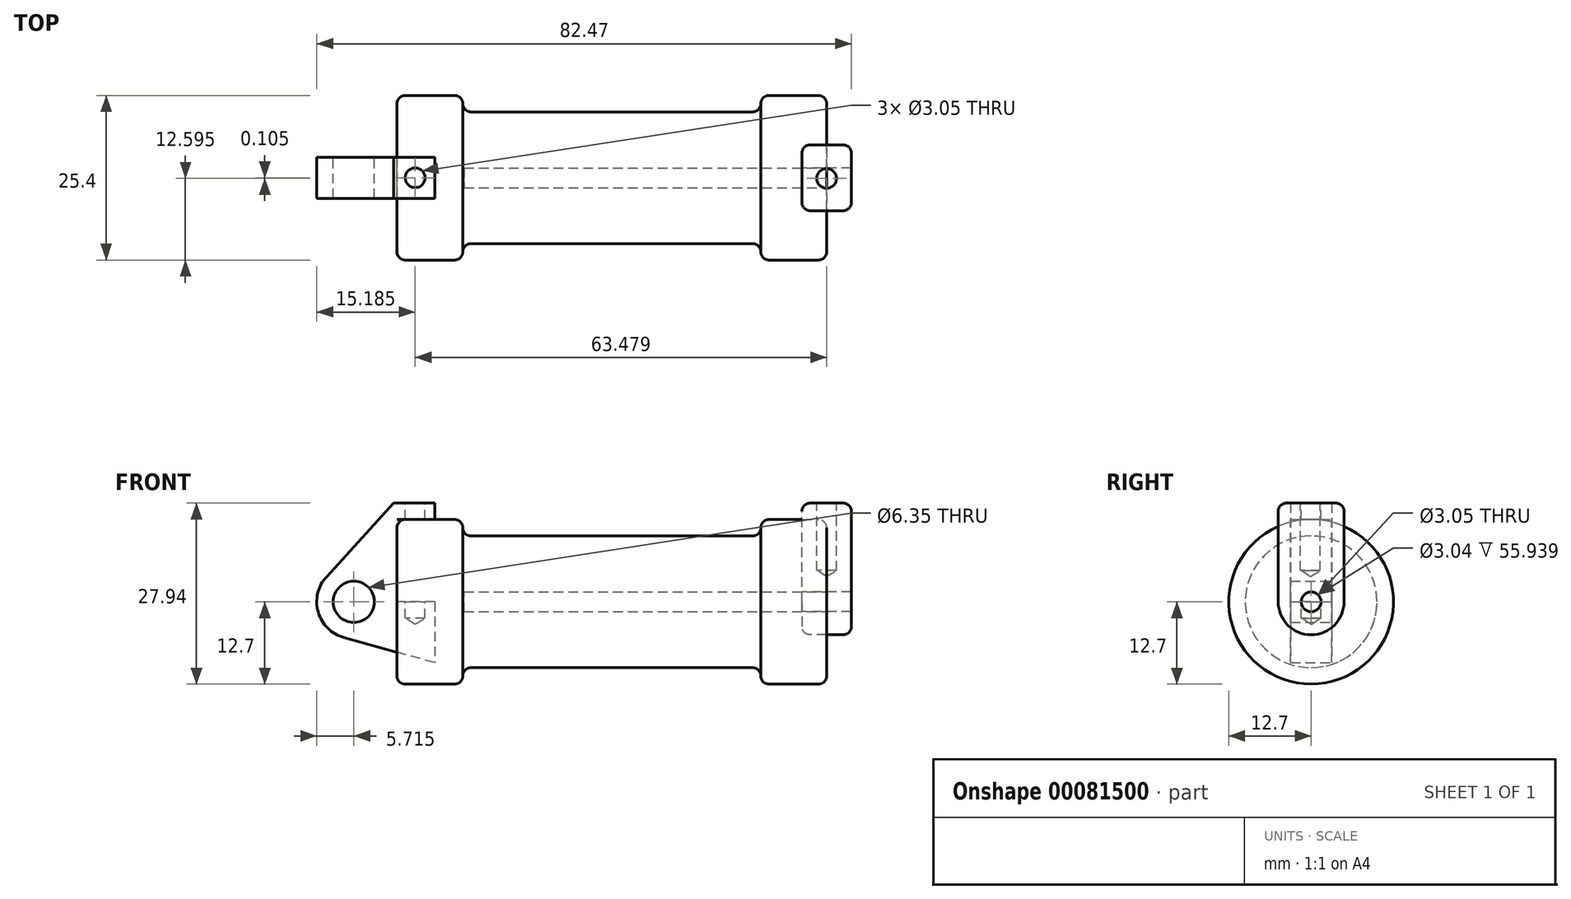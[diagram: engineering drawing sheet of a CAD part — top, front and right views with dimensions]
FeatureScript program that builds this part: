
annotation { "Feature Type Name" : "Feature", "Feature Type Description" : "" }
export const myFeature = defineFeature(function(context is Context, id is Id, definition is map)
    precondition{}
    {
        {
            var Q0;
            Q0=qCreatedBy(makeId("Front.planeOp"),FACE);
            var sketch = newSketch(context, id + "F0", { "sketchPlane" : qUnion([Q0])});
            skLineSegment(sketch, "E0", {"start": v(0, 0) * mm, "end": v(0, 12.7) * mm});
            skLineSegment(sketch, "E1", {"start": v(0, 12.7) * mm, "end": v(10.16, 12.7) * mm});
            skLineSegment(sketch, "E2", {"start": v(10.16, 12.7) * mm, "end": v(10.16, 10.16) * mm});
            skLineSegment(sketch, "E3", {"start": v(10.16, 10.16) * mm, "end": v(56.13, 10.16) * mm});
            skLineSegment(sketch, "E4", {"start": v(56.13, 10.16) * mm, "end": v(56.13, 12.7) * mm});
            skLineSegment(sketch, "E5", {"start": v(56.13, 12.7) * mm, "end": v(66.3, 12.7) * mm});
            skLineSegment(sketch, "E6", {"start": v(66.3, 12.7) * mm, "end": v(66.3, 0) * mm});
            skLineSegment(sketch, "E7", {"start": v(66.3, 0) * mm, "end": v(0, 0) * mm});
            skLineSegment(sketch, "E8", {"start": v(5.84, 15.24) * mm, "end": v(-0.5, 15.24) * mm});
            skLineSegment(sketch, "E9", {"start": v(-0.5, 15.24) * mm, "end": v(-10.88, 3.85) * mm});
            skLineSegment(sketch, "E10", {"start": v(0, 0) * mm, "end": v(-6.65, 0) * mm});
            skCircle(sketch, "E11", {"center": v(-6.65, 0) * mm, "radius": 5.72 * mm});
            skCircle(sketch, "E12", {"center": v(-6.65, 0) * mm, "radius": 3.18 * mm});
            skLineSegment(sketch, "E13", {"start": v(5.84, 15.24) * mm, "end": v(5.84, -9.4) * mm});
            skLineSegment(sketch, "E14", {"start": v(5.84, -9.4) * mm, "end": v(-8.18, -5.5) * mm});
            skSolve(sketch);
        }
        {
            var Q0;
            {var subQ0=sQuery(id+"F0.wireOp",EDGE,"E2");Q0=makeQuery(id+"F0.imprint","IMPRINT",FACE,{"disambiguationData":[TD([[makeQuery(id+"F0.imprint","IMPRINT",EDGE,{"derivedFrom":subQ0}),-1.0]])]});}
            var Q1;
            {var subQ0=sQuery(id+"F0.wireOp",EDGE,"E0");Q1=makeQuery(id+"F0.imprint","IMPRINT",FACE,{"disambiguationData":[TD([[makeQuery(id+"F0.imprint","IMPRINT",EDGE,{"derivedFrom":subQ0}),-1.0]])]});}
            var Q2;
            Q2=sQuery(id+"F0.wireOp",EDGE,"E7");
            revolve(context, id + "F1", {"entities" : qUnion([Q0, Q1]), "axis" : qUnion([Q2]), "revolveType" : RevolveType.FULL});
        }
        {
            var Q0;
            {var subQ3=sQuery(id+"F0.wireOp",EDGE,"E0");Q0=makeQuery(id+"F0.imprint","IMPRINT",FACE,{"disambiguationData":[TD([[makeQuery(id+"F0.imprint","IMPRINT",EDGE,{"derivedFrom":subQ3}),1.0]])]});}
            var Q1;
            {var subQ0=sQuery(id+"F0.wireOp",EDGE,"E14");Q1=makeQuery(id+"F0.imprint","IMPRINT",FACE,{"disambiguationData":[TD([[makeQuery(id+"F0.imprint","IMPRINT",EDGE,{"derivedFrom":subQ0}),-1.0]])]});}
            var Q2;
            {var subQ4=sQuery(id+"F0.wireOp",EDGE,"E12");Q2=makeQuery(id+"F0.imprint","IMPRINT",FACE,{"disambiguationData":[TD([[makeQuery(id+"F0.imprint","IMPRINT",EDGE,{"derivedFrom":subQ4}),-1.0]])]});}
            extrude(context, id + "F2", {"entities" : qUnion([Q0, Q1, Q2]), "endBound" : BoundingType.SYMMETRIC, "depth" : 6.35 * mm});
        }
        {
            var Q0;
            Q0=makeQuery(id+"F1.opRevolve","SWEPT_FACE",FACE,{"disambiguationData":[OSD([sQuery(id+"F0.wireOp",EDGE,"E6")])]});
            var sketch = newSketch(context, id + "F3", { "sketchPlane" : qUnion([Q0])});
            skCircle(sketch, "E15", {"center": v(0, 0) * mm, "radius": 5.08 * mm});
            skCircle(sketch, "E16", {"center": v(0, 0) * mm, "radius": 1.52 * mm});
            skLineSegment(sketch, "E17", {"start": v(-5.08, 0) * mm, "end": v(-5.08, 15.24) * mm});
            skLineSegment(sketch, "E18", {"start": v(5.08, 0) * mm, "end": v(5.08, 15.24) * mm});
            skLineSegment(sketch, "E19", {"start": v(-5.08, 15.24) * mm, "end": v(5.08, 15.24) * mm});
            skSolve(sketch);
        }
        {
            var Q0;
            Q0=makeQuery(id+"F3.imprint","IMPRINT",FACE,{"disambiguationData":[TD([[makeQuery(id+"F3.imprint","IMPRINT",EDGE,{"derivedFrom":sQuery(id+"F3.wireOp",EDGE,"E16")}),-1.0]])]});
            var Q1;
            {var subQ0=sQuery(id+"F3.wireOp",EDGE,"E19");Q1=makeQuery(id+"F3.imprint","IMPRINT",FACE,{"disambiguationData":[TD([[makeQuery(id+"F3.imprint","IMPRINT",EDGE,{"derivedFrom":subQ0}),-1.0]])]});}
            var Q2;
            {var subQ0=sQuery(id+"F3.wireOp",EDGE,"E17");var subQ1=sQuery(id+"F3.wireOp",EDGE,"E15");var subQ2=makeQuery(id+"F3.imprint","INTERSECT",VERTEX,{"derivedFrom":[subQ1,subQ0]});Q2=makeQuery(id+"F3.imprint","IMPRINT",FACE,{"disambiguationData":[TD([[makeQuery(id+"F3.imprint","IMPRINT",EDGE,{"disambiguationData":[TD([[subQ2,1.0]])],"derivedFrom":subQ1}),-1.0]])]});}
            extrude(context, id + "F4", {"entities" : qUnion([Q0, Q1, Q2]), "endBound" : BoundingType.SYMMETRIC, "depth" : 7.62 * mm});
        }
        {
            var Q0;
            Q0=makeQuery(id+"F4.opExtrude","CAP_FACE",FACE,{"disambiguationData":[OSD([sQuery(id+"F3.wireOp",EDGE,"E15"),sQuery(id+"F3.wireOp",EDGE,"E16"),sQuery(id+"F3.wireOp",EDGE,"E17"),sQuery(id+"F3.wireOp",EDGE,"E18"),sQuery(id+"F3.wireOp",EDGE,"E19")])],"isStart":false});
            var sketch = newSketch(context, id + "F5", { "sketchPlane" : qUnion([Q0])});
            skCircle(sketch, "E20", {"center": v(0, 0) * mm, "radius": 1.52 * mm});
            skSolve(sketch);
        }
        {
            var Q0;
            Q0 = qSketchRegion(id + "F5", true);
            extrude(context, id + "F6", {"entities" : qUnion([Q0]), "operationType" : NewBodyOperationType.REMOVE, "oppositeDirection" : true, "depth" : 59.75 * mm});
        }
        {
            var Q0;
            Q0=makeQuery(id+"F4.opExtrude","SWEPT_FACE",FACE,{"disambiguationData":[OSD([sQuery(id+"F3.wireOp",EDGE,"E19")])]});
            var sketch = newSketch(context, id + "F7", { "sketchPlane" : qUnion([Q0])});
            skCircle(sketch, "E21", {"center": v(66.3, -0.1) * mm, "radius": 1.52 * mm});
            skPoint(sketch, "E21.centerSnap0", {"position": v(66.3, -5.08) * mm});
            skSolve(sketch);
        }
        {
            var Q0;
            Q0=makeQuery(id+"F2.opExtrude","SWEPT_FACE",FACE,{"disambiguationData":[OSD([sQuery(id+"F0.wireOp",EDGE,"E8")])]});
            var sketch = newSketch(context, id + "F8", { "sketchPlane" : qUnion([Q0])});
            skCircle(sketch, "E22", {"center": v(2.82, 0) * mm, "radius": 1.52 * mm});
            skPoint(sketch, "E22.centerSnap0", {"position": v(-0.5, 0) * mm});
            skSolve(sketch);
        }
        {
            var Q0;
            Q0=sQuery(id+"F8.wireOp",VERTEX,"E22.center");
            var Q1;
            Q1=makeQuery(id+"F2.opExtrude","SWEPT_BODY",BODY,{"disambiguationData":[OSD([sQuery(id+"F0.wireOp",EDGE,"E0"),sQuery(id+"F0.wireOp",EDGE,"E1"),sQuery(id+"F0.wireOp",EDGE,"E7"),sQuery(id+"F0.wireOp",EDGE,"E8"),sQuery(id+"F0.wireOp",EDGE,"E9"),sQuery(id+"F0.wireOp",EDGE,"E11"),sQuery(id+"F0.wireOp",EDGE,"E12"),sQuery(id+"F0.wireOp",EDGE,"E13"),sQuery(id+"F0.wireOp",EDGE,"E14")])]});
            hole(context, id + "F9", {"style" : HoleStyle.SIMPLE, "endStyle" : HoleEndStyle.BLIND, "holeDiameter" : 3.05 * mm, "holeDepth" : 17.78 * mm, "locations" : qUnion([Q0]), "scope" : qUnion([Q1])});
        }
        {
            var Q0;
            Q0=sQuery(id+"F7.wireOp",VERTEX,"E21.center");
            var Q1;
            Q1=makeQuery(id+"F4.opExtrude","SWEPT_BODY",BODY,{"disambiguationData":[OSD([sQuery(id+"F3.wireOp",EDGE,"E15"),sQuery(id+"F3.wireOp",EDGE,"E16"),sQuery(id+"F3.wireOp",EDGE,"E17"),sQuery(id+"F3.wireOp",EDGE,"E18"),sQuery(id+"F3.wireOp",EDGE,"E19")])]});
            hole(context, id + "F10", {"style" : HoleStyle.SIMPLE, "endStyle" : HoleEndStyle.BLIND, "holeDiameter" : 3.05 * mm, "holeDepth" : 10.4 * mm, "locations" : qUnion([Q0]), "scope" : qUnion([Q1])});
        }
        {
            var Q0;
            Q0=makeQuery(id+"F1.opRevolve","SWEPT_EDGE",EDGE,{"disambiguationData":[OSD([sQuery(id+"F0.wireOp",EDGE,"E1"),sQuery(id+"F0.wireOp",EDGE,"E2")])]});
            var Q1;
            Q1=makeQuery(id+"F1.opRevolve","SWEPT_EDGE",EDGE,{"disambiguationData":[OSD([sQuery(id+"F0.wireOp",EDGE,"E2"),sQuery(id+"F0.wireOp",EDGE,"E3")])]});
            var Q2;
            Q2=makeQuery(id+"F1.opRevolve","SWEPT_EDGE",EDGE,{"disambiguationData":[OSD([sQuery(id+"F0.wireOp",EDGE,"E0"),sQuery(id+"F0.wireOp",EDGE,"E1")])]});
            var Q3;
            Q3=makeQuery(id+"F1.opRevolve","SWEPT_EDGE",EDGE,{"disambiguationData":[OSD([sQuery(id+"F0.wireOp",EDGE,"E4"),sQuery(id+"F0.wireOp",EDGE,"E5")])]});
            var Q4;
            Q4=makeQuery(id+"F1.opRevolve","SWEPT_EDGE",EDGE,{"disambiguationData":[OSD([sQuery(id+"F0.wireOp",EDGE,"E5"),sQuery(id+"F0.wireOp",EDGE,"E6")])]});
            var Q5;
            Q5=makeQuery(id+"F1.opRevolve","SWEPT_EDGE",EDGE,{"disambiguationData":[OSD([sQuery(id+"F0.wireOp",EDGE,"E3"),sQuery(id+"F0.wireOp",EDGE,"E4")])]});
            fillet(context, id + "F11", {"entities" : qUnion([Q0, Q1, Q2, Q3, Q4, Q5]), "radius" : 1.27 * mm, "tangentPropagation" : true, "allowEdgeOverflow" : false});
        }
        {
            var Q0;
            Q0=makeQuery(id+"F2.opExtrude","SWEPT_EDGE",EDGE,{"disambiguationData":[OSD([sQuery(id+"F0.wireOp",EDGE,"E8"),sQuery(id+"F0.wireOp",EDGE,"E13")])]});
            var Q1;
            Q1=makeQuery(id+"F2.opExtrude","SWEPT_EDGE",EDGE,{"disambiguationData":[OSD([sQuery(id+"F0.wireOp",EDGE,"E1"),sQuery(id+"F0.wireOp",EDGE,"E13")])]});
            var Q2;
            Q2=makeQuery(id+"F2.opExtrude","CAP_EDGE",EDGE,{"disambiguationData":[OSD([sQuery(id+"F0.wireOp",EDGE,"E1")])],"isStart":false});
            var Q3;
            Q3=makeQuery(id+"F2.opExtrude","CAP_EDGE",EDGE,{"disambiguationData":[OSD([sQuery(id+"F0.wireOp",EDGE,"E8")])],"isStart":false});
            var Q4;
            Q4=makeQuery(id+"F2.opExtrude","CAP_EDGE",EDGE,{"disambiguationData":[OSD([sQuery(id+"F0.wireOp",EDGE,"E9")])],"isStart":false});
            var Q5;
            Q5=makeQuery(id+"F2.opExtrude","CAP_EDGE",EDGE,{"disambiguationData":[OSD([sQuery(id+"F0.wireOp",EDGE,"E0")])],"isStart":false});
            var Q6;
            Q6=makeQuery(id+"F2.opExtrude","CAP_EDGE",EDGE,{"disambiguationData":[OSD([sQuery(id+"F0.wireOp",EDGE,"E12")])],"isStart":false});
            var Q7;
            Q7=makeQuery(id+"F2.opExtrude","CAP_EDGE",EDGE,{"disambiguationData":[OSD([sQuery(id+"F0.wireOp",EDGE,"E8")])],"isStart":true});
            var Q8;
            Q8=makeQuery(id+"F2.opExtrude","SWEPT_EDGE",EDGE,{"disambiguationData":[OSD([sQuery(id+"F0.wireOp",EDGE,"E8"),sQuery(id+"F0.wireOp",EDGE,"E9")])]});
            var Q9;
            Q9=makeQuery(id+"F2.opExtrude","CAP_EDGE",EDGE,{"disambiguationData":[OSD([sQuery(id+"F0.wireOp",EDGE,"E9")])],"isStart":true});
            var Q10;
            Q10=makeQuery(id+"F2.opExtrude","CAP_EDGE",EDGE,{"disambiguationData":[OSD([sQuery(id+"F0.wireOp",EDGE,"E14")])],"isStart":false});
            var Q11;
            Q11=makeQuery(id+"F2.opExtrude","CAP_EDGE",EDGE,{"disambiguationData":[OSD([sQuery(id+"F0.wireOp",EDGE,"E11")])],"isStart":false});
            var Q12;
            {var subQ0=sQuery(id+"F0.wireOp",EDGE,"E0");Q12=makeQuery(id+"F11.opFillet","BLEND_EDGE",EDGE,{"blendedFrom":[makeQuery(id+"F1.opRevolve","SWEPT_EDGE",EDGE,{"disambiguationData":[OSD([subQ0,sQuery(id+"F0.wireOp",EDGE,"E1")])]}),makeQuery(id+"F1.opRevolve","SWEPT_FACE",FACE,{"disambiguationData":[OSD([subQ0])]})],"blendedInto":[makeQuery(id+"F1.opRevolve","SWEPT_FACE",FACE,{"disambiguationData":[OSD([subQ0])]})]});}
            var Q13;
            Q13=makeQuery(id+"F2.opExtrude","CAP_EDGE",EDGE,{"disambiguationData":[OSD([sQuery(id+"F0.wireOp",EDGE,"E0")])],"isStart":true});
            fillet(context, id + "F12", {"entities" : qUnion([Q0, Q1, Q2, Q3, Q4, Q5, Q6, Q7, Q8, Q9, Q10, Q11, Q12, Q13]), "radius" : 1.27 * mm, "tangentPropagation" : true, "allowEdgeOverflow" : false});
        }
        {
            var Q0;
            Q0=makeQuery(id+"F4.opExtrude","CAP_EDGE",EDGE,{"disambiguationData":[OSD([sQuery(id+"F3.wireOp",EDGE,"E19")])],"isStart":true});
            var Q1;
            Q1=makeQuery(id+"F4.opExtrude","SWEPT_EDGE",EDGE,{"disambiguationData":[OSD([sQuery(id+"F3.wireOp",EDGE,"E18"),sQuery(id+"F3.wireOp",EDGE,"E19")])]});
            var Q2;
            Q2=makeQuery(id+"F4.opExtrude","CAP_EDGE",EDGE,{"disambiguationData":[OSD([sQuery(id+"F3.wireOp",EDGE,"E18")])],"isStart":true});
            var Q3;
            Q3=makeQuery(id+"F4.opExtrude","CAP_EDGE",EDGE,{"disambiguationData":[OSD([sQuery(id+"F3.wireOp",EDGE,"E18")])],"isStart":false});
            var Q4;
            Q4=makeQuery(id+"F4.opExtrude","CAP_EDGE",EDGE,{"disambiguationData":[OSD([sQuery(id+"F3.wireOp",EDGE,"E19")])],"isStart":false});
            var Q5;
            Q5=makeQuery(id+"F4.opExtrude","CAP_EDGE",EDGE,{"disambiguationData":[OSD([sQuery(id+"F3.wireOp",EDGE,"E17")])],"isStart":false});
            var Q6;
            Q6=makeQuery(id+"F4.opExtrude","CAP_EDGE",EDGE,{"disambiguationData":[OSD([sQuery(id+"F3.wireOp",EDGE,"E15")])],"isStart":false});
            var Q7;
            Q7=makeQuery(id+"F4.opExtrude","SWEPT_EDGE",EDGE,{"disambiguationData":[OSD([sQuery(id+"F3.wireOp",EDGE,"E17"),sQuery(id+"F3.wireOp",EDGE,"E19")])]});
            fillet(context, id + "F13", {"entities" : qUnion([Q0, Q1, Q2, Q3, Q4, Q5, Q6, Q7]), "radius" : 1.27 * mm, "tangentPropagation" : true, "allowEdgeOverflow" : false});
        }
    });
